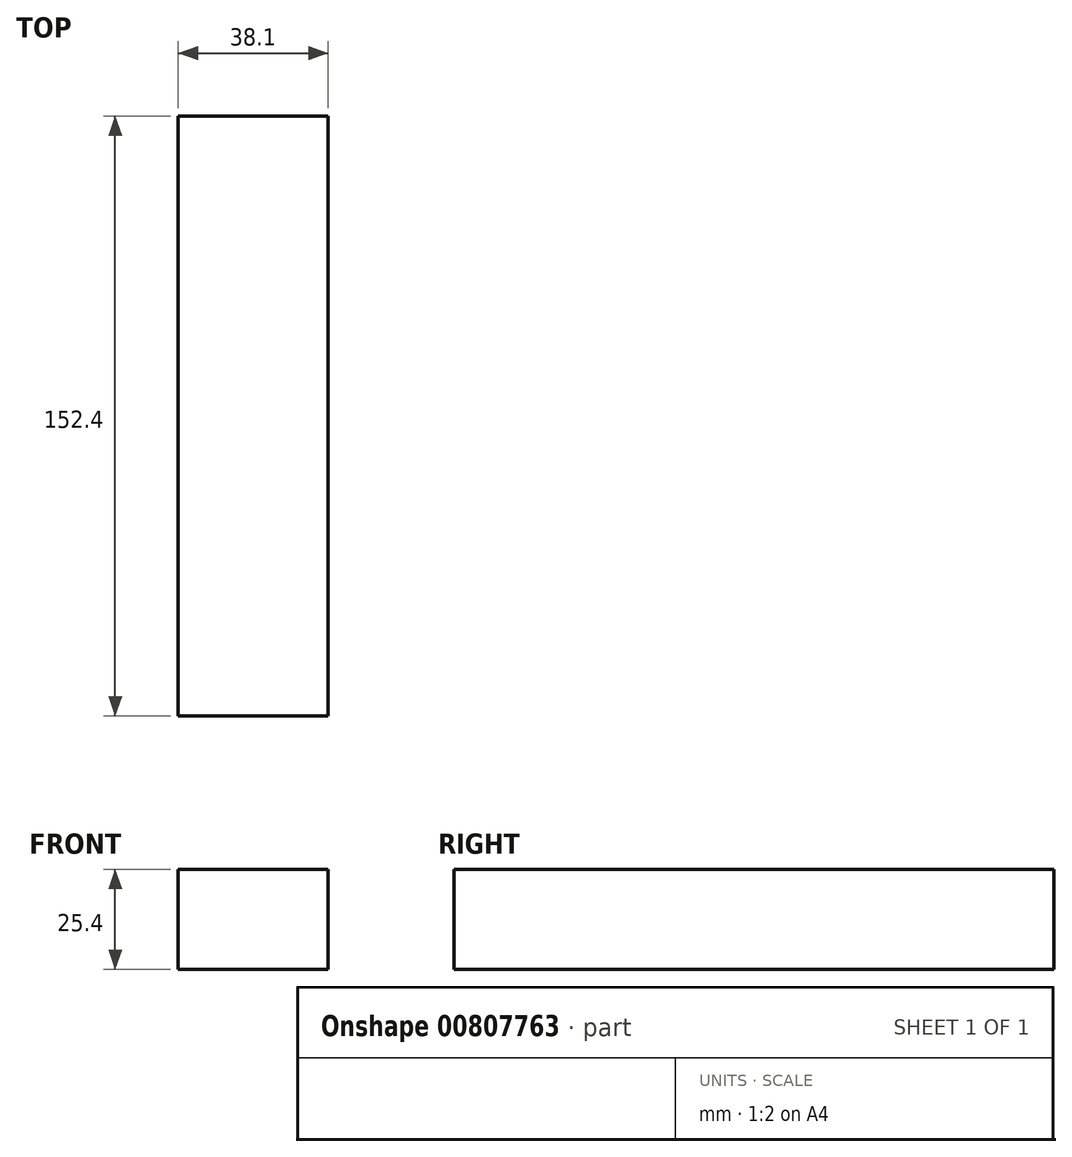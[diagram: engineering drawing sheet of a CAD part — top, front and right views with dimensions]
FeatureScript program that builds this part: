
annotation { "Feature Type Name" : "Feature", "Feature Type Description" : "" }
export const myFeature = defineFeature(function(context is Context, id is Id, definition is map)
    precondition{}
    {
        {
            var Q0;
            Q0=qCreatedBy(makeId("Right.planeOp"),FACE);
            var sketch = newSketch(context, id + "F0", { "sketchPlane" : qUnion([Q0])});
            skLineSegment(sketch, "E0.bottom", {"start": v(91.52, 15.62) * mm, "end": v(-60.88, 15.62) * mm});
            skLineSegment(sketch, "E0.top", {"start": v(91.52, -9.78) * mm, "end": v(-60.88, -9.78) * mm});
            skLineSegment(sketch, "E0.left", {"start": v(91.52, 15.62) * mm, "end": v(91.52, -9.78) * mm});
            skLineSegment(sketch, "E0.right", {"start": v(-60.88, 15.62) * mm, "end": v(-60.88, -9.78) * mm});
            skPoint(sketch, "E0.middle", {"position": v(15.32, 2.92) * mm});
            skSolve(sketch);
        }
        {
            var Q0;
            Q0=makeQuery(id+"F0.imprint","IMPRINT",FACE,{"disambiguationData":[TD([[makeQuery(id+"F0.imprint","IMPRINT",EDGE,{"derivedFrom":sQuery(id+"F0.wireOp",EDGE,"E0.bottom")}),1.0]])]});
            extrude(context, id + "F1", {"entities" : qUnion([Q0]), "depth" : 38.1 * mm, "offsetDistance" : 25.4 * mm});
        }
    });
